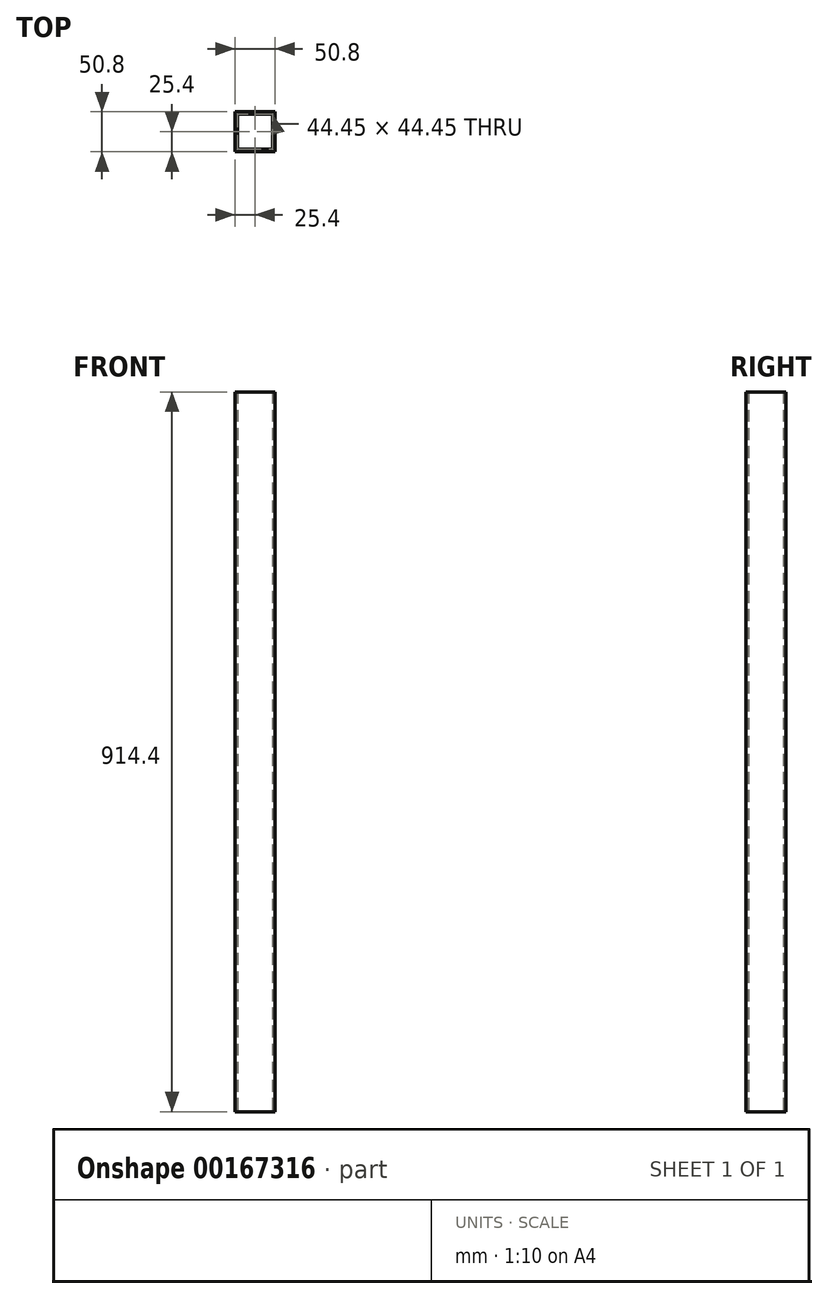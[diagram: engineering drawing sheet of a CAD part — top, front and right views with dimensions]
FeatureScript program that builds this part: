
annotation { "Feature Type Name" : "Feature", "Feature Type Description" : "" }
export const myFeature = defineFeature(function(context is Context, id is Id, definition is map)
    precondition{}
    {
        {
            var Q0;
            Q0=qCreatedBy(makeId("Top.planeOp"),FACE);
            var sketch = newSketch(context, id + "F0", { "sketchPlane" : qUnion([Q0])});
            skLineSegment(sketch, "E0.bottom", {"start": v(-25.4, 25.4) * mm, "end": v(25.4, 25.4) * mm});
            skLineSegment(sketch, "E0.top", {"start": v(-25.4, -25.4) * mm, "end": v(25.4, -25.4) * mm});
            skLineSegment(sketch, "E0.left", {"start": v(-25.4, 25.4) * mm, "end": v(-25.4, -25.4) * mm});
            skLineSegment(sketch, "E0.right", {"start": v(25.4, 25.4) * mm, "end": v(25.4, -25.4) * mm});
            skLineSegment(sketch, "E1.bottom", {"start": v(-22.23, 22.22) * mm, "end": v(22.22, 22.23) * mm});
            skLineSegment(sketch, "E1.top", {"start": v(-22.22, -22.23) * mm, "end": v(22.23, -22.22) * mm});
            skLineSegment(sketch, "E1.left", {"start": v(-22.23, 22.22) * mm, "end": v(-22.22, -22.23) * mm});
            skLineSegment(sketch, "E1.right", {"start": v(22.22, 22.23) * mm, "end": v(22.23, -22.23) * mm});
            skSolve(sketch);
        }
        {
            var Q0;
            Q0 = qSketchRegion(id + "F0", true);
            extrude(context, id + "F1", {"entities" : qUnion([Q0]), "depth" : 914.4 * mm});
        }
    });
